# Revit family: Electronics_Commercial-Loudspeakers_Biamp_Small-Design-Loudspeaker_OVO3T
name_source: partatom
category: Communication Devices
units: mm (PartAtom-declared; Revit-internal decimal feet)

## family parameters
Cut with Voids When Loaded = No
Host = Face
Maintain Annotation Orientation = No
OmniClass Number = 23.85.10.11.14.14.14
Part Type = Normal
Room Calculation Point = No
Round Connector Dimension = Use Diameter
Shared = No

## types (2) — shared parameters
Compliance = IEC 62368-1 certified
Connector Description = Spring terminals; 18 V 20 W 16 Ω Nominal Impedance, 70/100V operation
Controls = Wattage / low impedance selector switch
Default Elevation = 48 "
Depth = 4.67 "
Environmental Rating = IP40 per IEC 60529
Height = 6.31 "
Input Connection = Spring-lever terminals with wiring cover
Manufacturer = Biamp
Mounting Provisions = Pan-tilt bracket and rubber tabletop stand
Nominal Beamwidth  (H x V) = 185° x 135°
Nominal Continuous Power Handling = 18 V  (20 W, 16 Ω Nominal Impedance)
Nominal Maximum SPL (Processed) = Peak: 93 dB - Continuous: 99 dB
Operating Environment = Indoor
Operating Mode = Passive with selectable low-impedance or 70V/100V operation, single amplified with DSP
Operating Range (-10 dB) = 100 Hz to 20 kHz
Product Documentation Link = https://downloads.biamp.com
Product Page URL = https://www.biamp.com
Product data url = https://bimobject.com
Rated Continuous Voltage = 17.8 V (25 dBV)
Rated Maximum SPL (Processed) = Peak: 93 dB - Continuous: 105 dB
Recommended Amplifiers = 20 W - 40 W, into 16 Ω (18 V - 25 V)
Required Accessories = 90 Hz, 12 dB / oct. Butterworth high pass filter; DSP preset
Sensitivity = 83 dB (2.83 V); 86 dB (1 W, 16 Ω)
Shipping Weight = 7.05 lbf
Transducers = LF 1 x 3 (76mm) coated paper cone, HF 1 x 1 (25 mm) silk dome driver
Transformer = 70 V: 6 W, 3 W, 1.5 W, 0.75 W;  100 V: 6 W, 3 W, 1.5 W
URL = https://www.biamp.com
Weight = 2.40 lbf
Width = 4.24 "

## per-type parameters (varying)
| type | Description | Grill Material | Housing Material |
| OVO3T B | OVO3T-B 3" Small Design Loudspeaker, Black | Biamp - Plastic - Black(Grid) | Biamp - Plastic - Black |
| OVO3T W | OVO3T-W 3" Small Design Loudspeaker, White | Biamp - Plastic - White(Grid) | Biamp - Plastic - White |

note: column(s) folded — value = type name in every type: Model

## geometry (parser evidence)
native form markers: Sweep x7
no freeform markers — native parametric forms only
